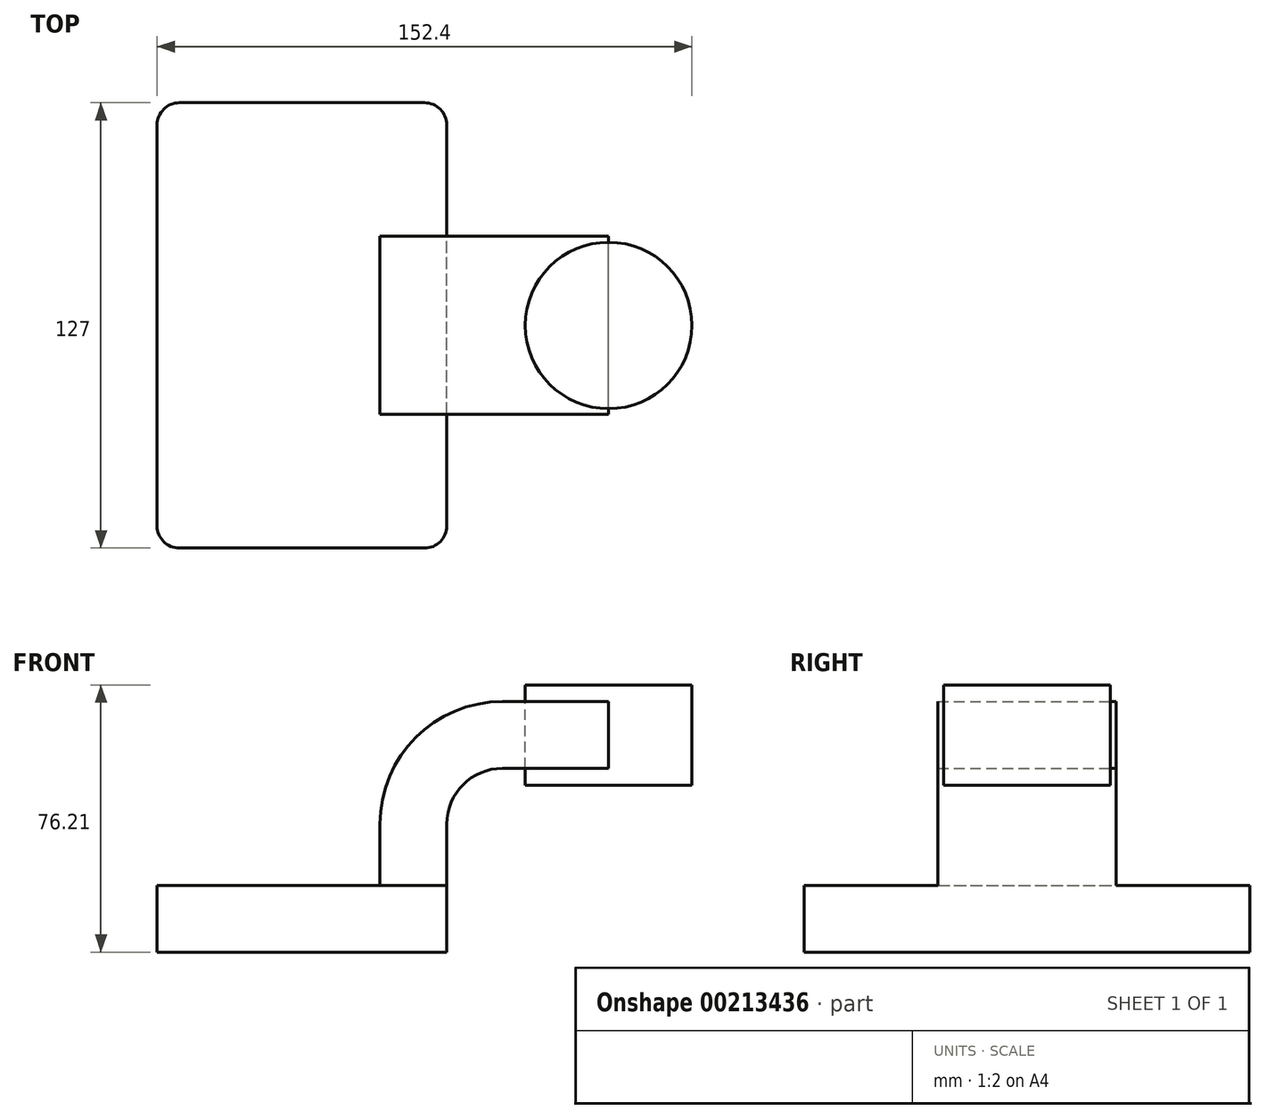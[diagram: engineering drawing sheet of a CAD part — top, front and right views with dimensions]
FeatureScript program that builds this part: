
annotation { "Feature Type Name" : "Feature", "Feature Type Description" : "" }
export const myFeature = defineFeature(function(context is Context, id is Id, definition is map)
    precondition{}
    {
        {
            var Q0;
            Q0=qCreatedBy(makeId("Front.planeOp"),FACE);
            var sketch = newSketch(context, id + "F0", { "sketchPlane" : qUnion([Q0])});
            skLineSegment(sketch, "E0.bottom", {"start": v(-41.28, -9.53) * mm, "end": v(41.28, -9.53) * mm});
            skLineSegment(sketch, "E0.top", {"start": v(-41.28, 9.53) * mm, "end": v(41.28, 9.53) * mm});
            skLineSegment(sketch, "E0.left", {"start": v(-41.28, -9.53) * mm, "end": v(-41.28, 9.53) * mm});
            skLineSegment(sketch, "E0.right", {"start": v(41.28, -9.53) * mm, "end": v(41.28, 9.53) * mm});
            skPoint(sketch, "E0.middle", {"position": v(0, 0) * mm});
            skLineSegment(sketch, "E1.bottom", {"start": v(60.32, 38.1) * mm, "end": v(111.12, 38.1) * mm});
            skLineSegment(sketch, "E1.top", {"start": v(60.32, 66.67) * mm, "end": v(111.12, 66.67) * mm});
            skLineSegment(sketch, "E1.left", {"start": v(60.32, 38.1) * mm, "end": v(60.32, 66.67) * mm});
            skLineSegment(sketch, "E1.right", {"start": v(111.12, 38.1) * mm, "end": v(111.12, 66.67) * mm});
            skPoint(sketch, "E1.middle", {"position": v(85.72, 52.39) * mm});
            skLineSegment(sketch, "E2", {"start": v(41.28, 9.53) * mm, "end": v(41.28, 27) * mm});
            skArc(sketch, "E3", {"start": v(41.27, 27) * mm, "mid": v(45.92, 38.23) * mm, "end": v(57.15, 42.88) * mm});
            skLineSegment(sketch, "E4", {"start": v(57.15, 42.88) * mm, "end": v(87.4, 42.88) * mm});
            skLineSegment(sketch, "E5.0", {"start": v(57.15, 61.93) * mm, "end": v(87.4, 61.93) * mm});
            skArc(sketch, "E5.1", {"start": v(22.22, 27) * mm, "mid": v(32.45, 51.7) * mm, "end": v(57.15, 61.93) * mm});
            skLineSegment(sketch, "E5.2", {"start": v(22.22, 9.53) * mm, "end": v(22.22, 27) * mm});
            skLineSegment(sketch, "E6", {"start": v(87.4, 66.67) * mm, "end": v(87.4, 38.1) * mm});
            skFitSpline(sketch, "E7", {"points": [v(-41.28, 9.53) * mm, v(57.15, 61.93) * mm], "startDerivative": vector(44.57, 62.11) * mm, "endDerivative": vector(129.84, -5.81) * mm});
            skSolve(sketch);
        }
        {
            var Q0;
            Q0=makeQuery(id+"F0.imprint","IMPRINT",FACE,{"disambiguationData":[TD([[makeQuery(id+"F0.imprint","IMPRINT",EDGE,{"derivedFrom":sQuery(id+"F0.wireOp",EDGE,"E0.bottom")}),1.0]])]});
            extrude(context, id + "F1", {"entities" : qUnion([Q0]), "endBound" : BoundingType.SYMMETRIC, "depth" : 127 * mm});
        }
        {
            var Q0;
            {var subQ1=sQuery(id+"F0.wireOp",EDGE,"E2");Q0=makeQuery(id+"F0.imprint","IMPRINT",FACE,{"disambiguationData":[TD([[makeQuery(id+"F0.imprint","IMPRINT",EDGE,{"derivedFrom":subQ1}),1.0]])]});}
            var Q1;
            {var subQ0=sQuery(id+"F0.wireOp",EDGE,"E4");var subQ1=sQuery(id+"F0.wireOp",EDGE,"E1.left");var subQ2=makeQuery(id+"F0.imprint","INTERSECT",VERTEX,{"derivedFrom":[subQ1,subQ0]});Q1=makeQuery(id+"F0.imprint","IMPRINT",FACE,{"disambiguationData":[TD([[makeQuery(id+"F0.imprint","IMPRINT",EDGE,{"disambiguationData":[TD([[subQ2,-1.0]])],"derivedFrom":subQ1}),-1.0]])]});}
            extrude(context, id + "F2", {"entities" : qUnion([Q0, Q1]), "operationType" : NewBodyOperationType.ADD, "endBound" : BoundingType.SYMMETRIC, "depth" : 50.8 * mm});
        }
        {
            var Q0;
            Q0=makeQuery(id+"F0.imprint","IMPRINT",FACE,{"disambiguationData":[TD([[makeQuery(id+"F0.imprint","IMPRINT",EDGE,{"derivedFrom":sQuery(id+"F0.wireOp",EDGE,"E5.1")}),1.0]])]});
            extrude(context, id + "F3", {"entities" : qUnion([Q0]), "operationType" : NewBodyOperationType.ADD, "depth" : 15.88 * mm});
        }
        {
            var Q0;
            {var subQ0=sQuery(id+"F0.wireOp",EDGE,"E1.right");Q0=makeQuery(id+"F0.imprint","IMPRINT",FACE,{"disambiguationData":[TD([[makeQuery(id+"F0.imprint","IMPRINT",EDGE,{"derivedFrom":subQ0}),1.0]])]});}
            var Q1;
            Q1=sQuery(id+"F0.wireOp",EDGE,"E6");
            revolve(context, id + "F4", {"entities" : qUnion([Q0]), "axis" : qUnion([Q1]), "revolveType" : RevolveType.FULL});
        }
        {
            var Q0;
            Q0=makeQuery(id+"F1.opExtrude","CAP_EDGE",EDGE,{"disambiguationData":[OSD([sQuery(id+"F0.wireOp",EDGE,"E0.left")])],"isStart":false});
            var Q1;
            Q1=makeQuery(id+"F1.opExtrude","CAP_EDGE",EDGE,{"disambiguationData":[OSD([sQuery(id+"F0.wireOp",EDGE,"E0.right")])],"isStart":true});
            var Q2;
            Q2=makeQuery(id+"F1.opExtrude","CAP_EDGE",EDGE,{"disambiguationData":[OSD([sQuery(id+"F0.wireOp",EDGE,"E0.right")])],"isStart":false});
            var Q3;
            Q3=makeQuery(id+"F1.opExtrude","CAP_EDGE",EDGE,{"disambiguationData":[OSD([sQuery(id+"F0.wireOp",EDGE,"E0.left")])],"isStart":true});
            fillet(context, id + "F5", {"entities" : qUnion([Q0, Q1, Q2, Q3]), "radius" : 6.35 * mm, "tangentPropagation" : true, "allowEdgeOverflow" : false});
        }
    });
